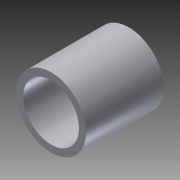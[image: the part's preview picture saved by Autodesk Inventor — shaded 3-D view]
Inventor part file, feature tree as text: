
AUTODESK INVENTOR PART (.ipt)
format: ipt  version: 2014 SP1 (Build 180222100, 222)  size: 86,016 bytes
history: native  units: in
note: dims shown in document units (in); Inventor stores cm internally (conversion verified against a paired STEP export)
features: extrude x1, sketch x1
ambient origin geometry x8: Origin, YZ Plane, XZ Plane, XY Plane, X Axis, Y Axis, Z Axis, Center Point
bodies: Solid1 (feature_tree)
feature tree (2):
  extrude  "Extrusion1"  Depth=0.698in
  sketch  "Sketch1"  dims[d0=0.625in d1=0.5in d2=0.698in d3=0.0in]
